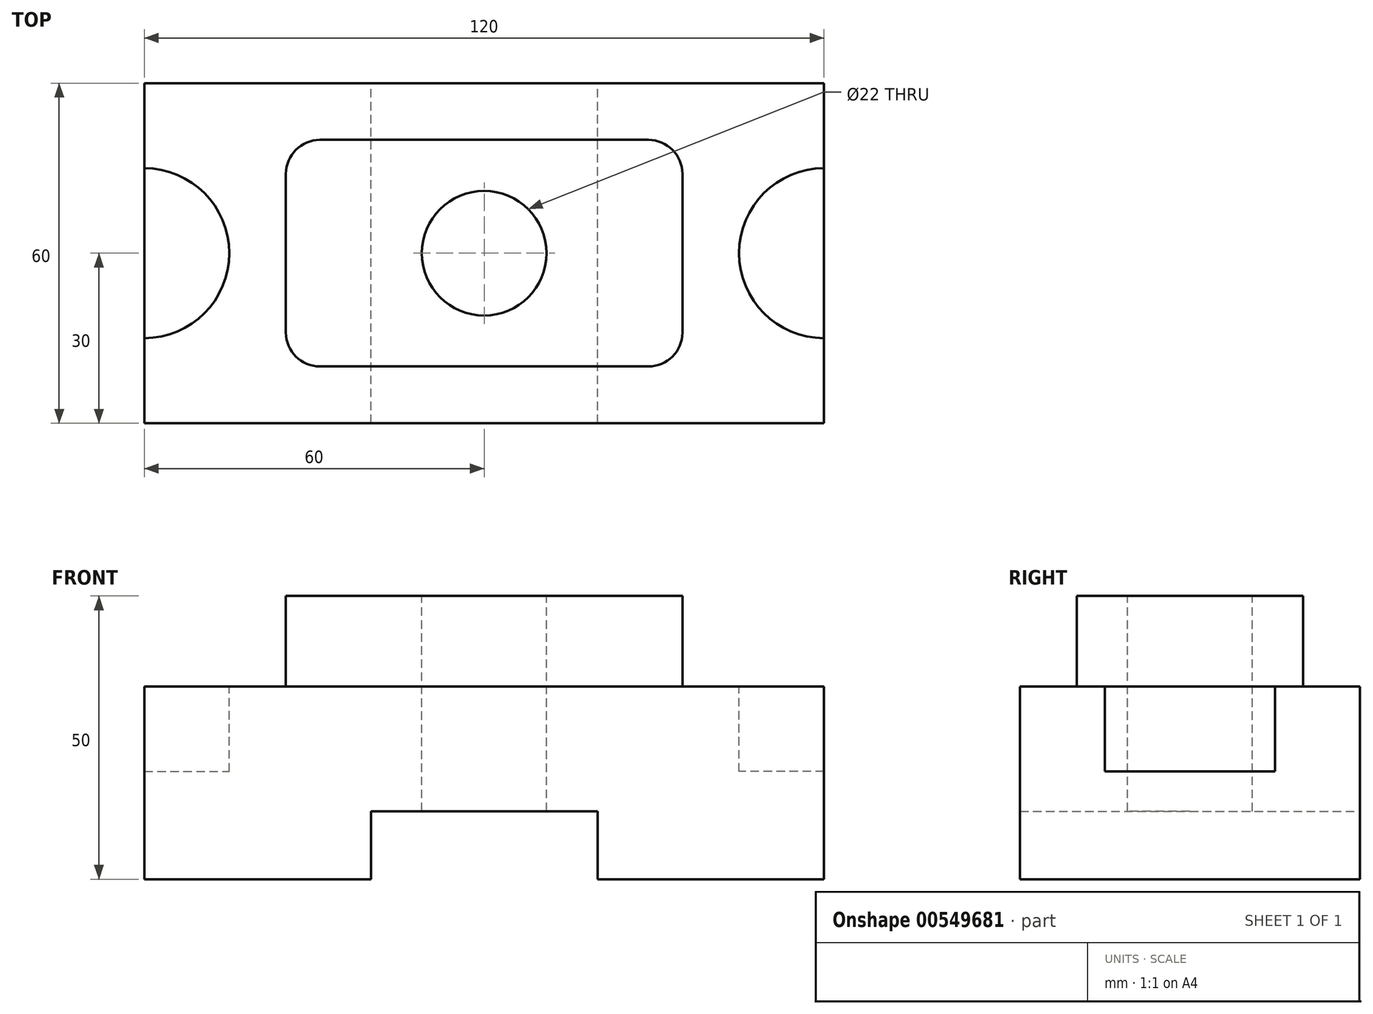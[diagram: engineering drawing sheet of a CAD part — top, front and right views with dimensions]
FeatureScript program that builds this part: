
annotation { "Feature Type Name" : "Feature", "Feature Type Description" : "" }
export const myFeature = defineFeature(function(context is Context, id is Id, definition is map)
    precondition{}
    {
        {
            var Q0;
            Q0=qCreatedBy(makeId("Top.planeOp"),FACE);
            var sketch = newSketch(context, id + "F0", { "sketchPlane" : qUnion([Q0])});
            skLineSegment(sketch, "E0.bottom", {"start": v(60, -30) * mm, "end": v(-60, -30) * mm});
            skLineSegment(sketch, "E0.top", {"start": v(60, 30) * mm, "end": v(-60, 30) * mm});
            skLineSegment(sketch, "E0.left", {"start": v(60, -30) * mm, "end": v(60, 30) * mm});
            skLineSegment(sketch, "E0.right", {"start": v(-60, -30) * mm, "end": v(-60, 30) * mm});
            skPoint(sketch, "E0.middle", {"position": v(0, 0) * mm});
            skSolve(sketch);
        }
        {
            var Q0;
            Q0 = qSketchRegion(id + "F0", true);
            extrude(context, id + "F1", {"entities" : qUnion([Q0]), "depth" : (50 - 16) * mm, "offsetDistance" : 25 * mm});
        }
        {
            var Q0;
            Q0=makeQuery(id+"F1.opExtrude","CAP_FACE",FACE,{"disambiguationData":[OSD([sQuery(id+"F0.wireOp",EDGE,"E0.bottom"),sQuery(id+"F0.wireOp",EDGE,"E0.top"),sQuery(id+"F0.wireOp",EDGE,"E0.left"),sQuery(id+"F0.wireOp",EDGE,"E0.right")])],"isStart":false});
            var sketch = newSketch(context, id + "F2", { "sketchPlane" : qUnion([Q0])});
            skLineSegment(sketch, "E1.bottom", {"start": v(35, -20) * mm, "end": v(-35, -20) * mm});
            skLineSegment(sketch, "E1.top", {"start": v(35, 20) * mm, "end": v(-35, 20) * mm});
            skLineSegment(sketch, "E1.left", {"start": v(35, -20) * mm, "end": v(35, 20) * mm});
            skLineSegment(sketch, "E1.right", {"start": v(-35, -20) * mm, "end": v(-35, 20) * mm});
            skPoint(sketch, "E1.middle", {"position": v(0, 0) * mm});
            skSolve(sketch);
        }
        {
            var Q0;
            Q0=makeQuery(id+"F2.imprint","IMPRINT",FACE,{"disambiguationData":[TD([[makeQuery(id+"F2.imprint","IMPRINT",EDGE,{"derivedFrom":sQuery(id+"F2.wireOp",EDGE,"E1.bottom")}),-1.0]])]});
            extrude(context, id + "F3", {"entities" : qUnion([Q0]), "operationType" : NewBodyOperationType.ADD, "depth" : 16 * mm, "offsetDistance" : 25 * mm});
        }
        {
            var Q0;
            Q0=makeQuery(id+"F3.opExtrude","SWEPT_EDGE",EDGE,{"disambiguationData":[OSD([sQuery(id+"F2.wireOp",EDGE,"E1.bottom"),sQuery(id+"F2.wireOp",EDGE,"E1.right")])]});
            var Q1;
            Q1=makeQuery(id+"F3.opExtrude","SWEPT_EDGE",EDGE,{"disambiguationData":[OSD([sQuery(id+"F2.wireOp",EDGE,"E1.top"),sQuery(id+"F2.wireOp",EDGE,"E1.right")])]});
            var Q2;
            Q2=makeQuery(id+"F3.opExtrude","SWEPT_EDGE",EDGE,{"disambiguationData":[OSD([sQuery(id+"F2.wireOp",EDGE,"E1.bottom"),sQuery(id+"F2.wireOp",EDGE,"E1.left")])]});
            var Q3;
            Q3=makeQuery(id+"F3.opExtrude","SWEPT_EDGE",EDGE,{"disambiguationData":[OSD([sQuery(id+"F2.wireOp",EDGE,"E1.top"),sQuery(id+"F2.wireOp",EDGE,"E1.left")])]});
            fillet(context, id + "F4", {"entities" : qUnion([Q0, Q1, Q2, Q3]), "radius" : 6 * mm, "tangentPropagation" : true, "allowEdgeOverflow" : false});
        }
        {
            var Q0;
            Q0=makeQuery(id+"F3.opExtrude","CAP_FACE",FACE,{"disambiguationData":[OSD([sQuery(id+"F2.wireOp",EDGE,"E1.bottom"),sQuery(id+"F2.wireOp",EDGE,"E1.top"),sQuery(id+"F2.wireOp",EDGE,"E1.left"),sQuery(id+"F2.wireOp",EDGE,"E1.right")])],"isStart":false});
            var sketch = newSketch(context, id + "F5", { "sketchPlane" : qUnion([Q0])});
            skCircle(sketch, "E2", {"center": v(0, 0) * mm, "radius": 11 * mm});
            skSolve(sketch);
        }
        {
            var Q0;
            Q0 = qSketchRegion(id + "F5", true);
            extrude(context, id + "F6", {"entities" : qUnion([Q0]), "operationType" : NewBodyOperationType.REMOVE, "endBound" : BoundingType.THROUGH_ALL, "oppositeDirection" : true, "depth" : 25 * mm, "offsetDistance" : 25 * mm});
        }
        {
            var Q0;
            Q0=makeQuery(id+"F1.opExtrude","CAP_FACE",FACE,{"disambiguationData":[OSD([sQuery(id+"F0.wireOp",EDGE,"E0.bottom"),sQuery(id+"F0.wireOp",EDGE,"E0.top"),sQuery(id+"F0.wireOp",EDGE,"E0.left"),sQuery(id+"F0.wireOp",EDGE,"E0.right")])],"isStart":false});
            var sketch = newSketch(context, id + "F7", { "sketchPlane" : qUnion([Q0])});
            skCircle(sketch, "E3", {"center": v(60, 0) * mm, "radius": 15 * mm});
            skCircle(sketch, "E4", {"center": v(-60, 0) * mm, "radius": 15 * mm});
            skSolve(sketch);
        }
        {
            var Q0;
            Q0 = qSketchRegion(id + "F7", true);
            extrude(context, id + "F8", {"entities" : qUnion([Q0]), "operationType" : NewBodyOperationType.REMOVE, "oppositeDirection" : true, "depth" : 15 * mm, "offsetDistance" : 25 * mm});
        }
        {
            var Q0;
            Q0=makeQuery(id+"F1.opExtrude","SWEPT_FACE",FACE,{"disambiguationData":[OSD([sQuery(id+"F0.wireOp",EDGE,"E0.top")])]});
            var sketch = newSketch(context, id + "F9", { "sketchPlane" : qUnion([Q0])});
            skLineSegment(sketch, "E5", {"start": v(-20, 0) * mm, "end": v(-20, 12) * mm});
            skLineSegment(sketch, "E6", {"start": v(-20, 12) * mm, "end": v(20, 12) * mm});
            skLineSegment(sketch, "E7", {"start": v(20, 12) * mm, "end": v(20, 0) * mm});
            skPoint(sketch, "E8", {"position": v(0, 12) * mm});
            skSolve(sketch);
        }
        {
            var Q0;
            Q0 = qSketchRegion(id + "F9", true);
            var Q1;
            {var subQ0=sQuery(id+"F9.wireOp",EDGE,"E5");Q1=makeQuery(id+"F9.imprint","IMPRINT",FACE,{"disambiguationData":[TD([[makeQuery(id+"F9.imprint","IMPRINT",EDGE,{"derivedFrom":subQ0}),-1.0]])]});}
            extrude(context, id + "F10", {"entities" : qUnion([Q0, Q1]), "operationType" : NewBodyOperationType.REMOVE, "endBound" : BoundingType.THROUGH_ALL, "oppositeDirection" : true, "depth" : 25 * mm, "offsetDistance" : 25 * mm});
        }
    });
